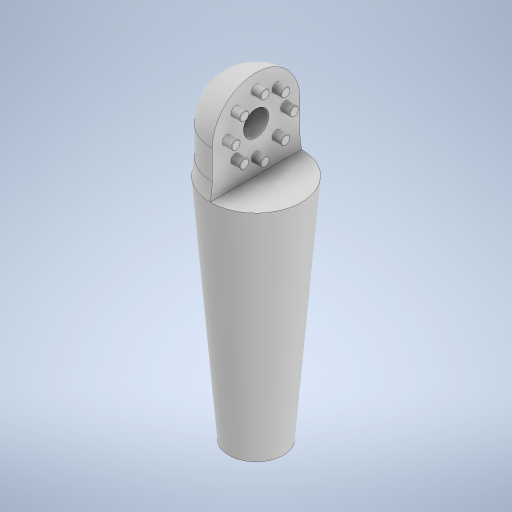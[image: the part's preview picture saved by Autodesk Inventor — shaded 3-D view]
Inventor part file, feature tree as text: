
AUTODESK INVENTOR PART (.ipt)
format: ipt  version: 2024 (Build 280153000, 153)  size: 523,264 bytes
history: native  units: in
note: dims shown in document units (in); Inventor stores cm internally (conversion verified against a paired STEP export)
features: sketch x6, extrude x4, fillet x3, plane x1, loft x1, thicken_offset x1
ambient origin geometry x8: Origin, YZ Plane, XZ Plane, XY Plane, X Axis, Y Axis, Z Axis, Center Point
bodies: Solid1 (feature_tree)
feature tree (16):
  sketch  "Sketch1"  dims[d0=0.6in d2=2.5in]
  plane  "Work Plane1"
  loft  "Loft1"
  extrude  "Extrusion1"  TaperAngle=0.0deg  [1 undecoded]
  extrude  "Extrusion2"  Depth=0.1in TaperAngle=0.0deg
  fillet  "Fillet1"  Radius=0.1in
  fillet  "Fillet2"  Radius=3.1496in
  extrude  "Extrusion3"  Depth=0.005in
  extrude  "Extrusion4"  Depth=0.3in
  thicken_offset  "Thicken1"
  fillet  "Fillet3"  Radius=0.3in
  sketch  "Sketch2"  dims[d3=1.0in d4=0.0in d5=90.0deg]
  sketch  "Sketch3"  dims[d6=0.0in d7=90.0deg d8=1.0in d9=0.0in d12=0.1in d13=3.1496in d15=360.0deg]
  sketch  "Sketch4"  dims[d17=0.1in d18=0.0in d19=0.005in]
  sketch  "Sketch5"  dims[d20=0.5in d21=0.2755in d22=0.3in d23=0.0in]
  sketch  "Sketch6"  dims[d24=0.4126in d25=2.0in d26=0.0in d29=0.02in d30=0.02in d31=0.875in d27=0.0344in d28=0.0344in]
note: 1 required parameter value undecoded (feature->parameter linkage not recoverable at this tier; creation-order binding heuristic only, values carry confidence <= 0.55)
